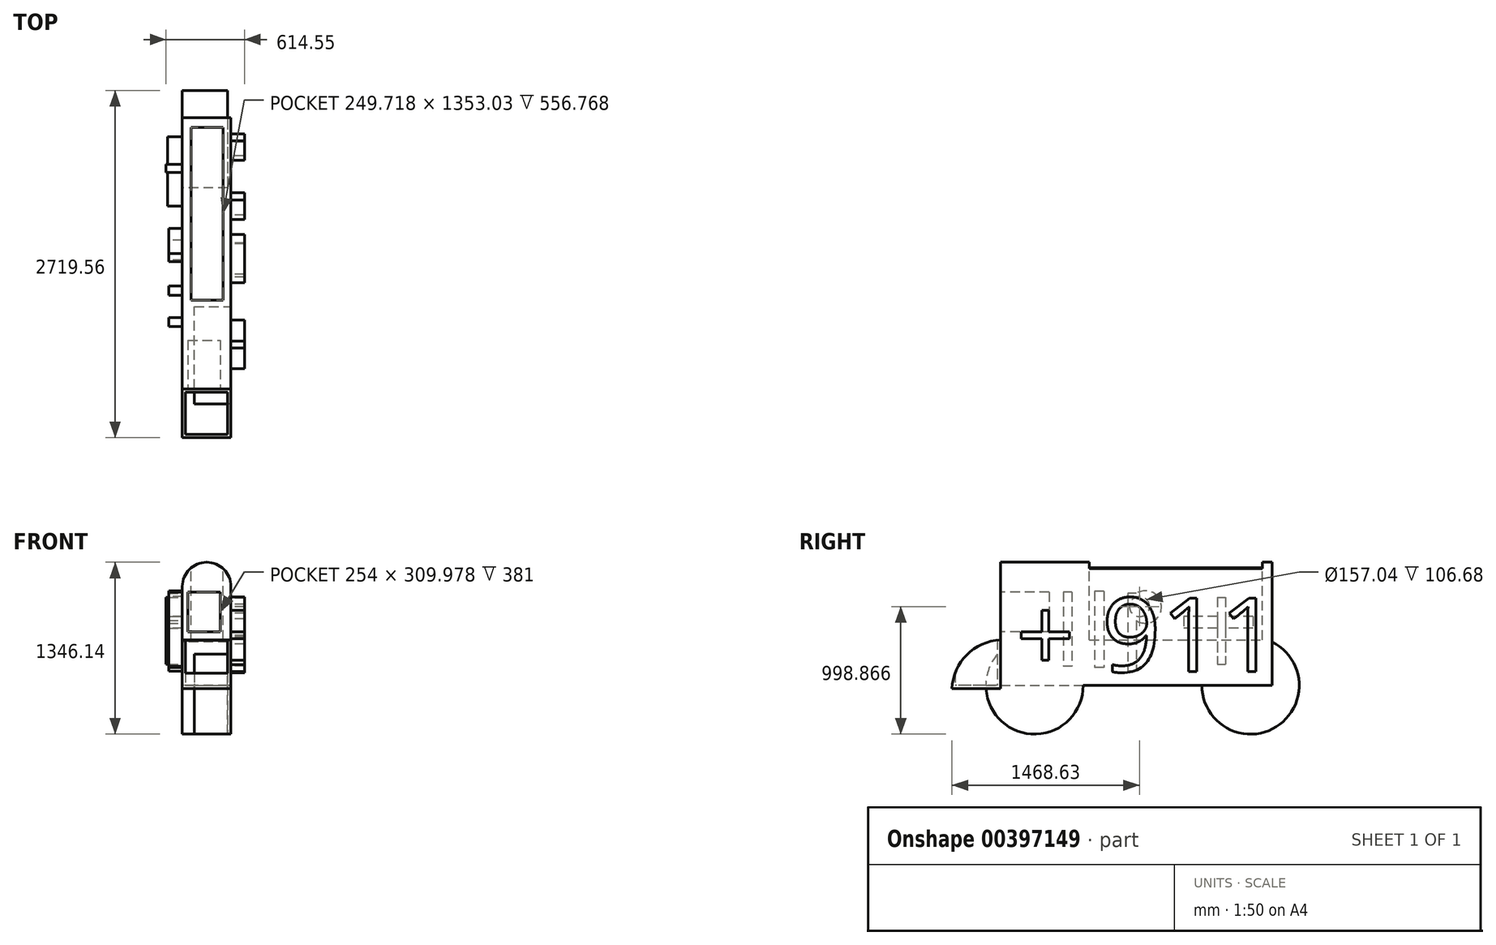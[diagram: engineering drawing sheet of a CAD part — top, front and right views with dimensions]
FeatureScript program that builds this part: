
annotation { "Feature Type Name" : "Feature", "Feature Type Description" : "" }
export const myFeature = defineFeature(function(context is Context, id is Id, definition is map)
    precondition{}
    {
        {
            var Q0;
            Q0=qCreatedBy(makeId("Top.planeOp"),FACE);
            var sketch = newSketch(context, id + "F0", { "sketchPlane" : qUnion([Q0])});
            skLineSegment(sketch, "E0.bottom", {"start": v(-196.72, 208.75) * mm, "end": v(184.28, 208.75) * mm});
            skLineSegment(sketch, "E0.top", {"start": v(-196.72, -172.25) * mm, "end": v(184.28, -172.25) * mm});
            skLineSegment(sketch, "E0.left", {"start": v(-196.72, 208.75) * mm, "end": v(-196.72, -172.25) * mm});
            skLineSegment(sketch, "E0.right", {"start": v(184.28, 208.75) * mm, "end": v(184.28, -172.25) * mm});
            skSolve(sketch);
        }
        {
            var Q0;
            Q0 = qSketchRegion(id + "F0", true);
            extrude(context, id + "F1", {"entities" : qUnion([Q0]), "depth" : 381 * mm});
        }
        {
            var Q0;
            Q0=makeQuery(id+"F1.opExtrude","CAP_FACE",FACE,{"disambiguationData":[OSD([sQuery(id+"F0.wireOp",EDGE,"E0.bottom"),sQuery(id+"F0.wireOp",EDGE,"E0.top"),sQuery(id+"F0.wireOp",EDGE,"E0.left"),sQuery(id+"F0.wireOp",EDGE,"E0.right")])],"isStart":false});
            shell(context, id + "F2", {"entities" : qUnion([Q0]), "thickness" : 25.4 * mm});
        }
        {
            var Q0;
            Q0=makeQuery(id+"F1.opExtrude","CAP_EDGE",EDGE,{"disambiguationData":[OSD([sQuery(id+"F0.wireOp",EDGE,"E0.top")])],"isStart":false});
            fillet(context, id + "F3", {"entities" : qUnion([Q0]), "radius" : 398.59 * mm, "tangentPropagation" : true, "allowEdgeOverflow" : false});
        }
        {
            var Q0;
            Q0=makeQuery(id+"F1.opExtrude","SWEPT_FACE",FACE,{"disambiguationData":[OSD([sQuery(id+"F0.wireOp",EDGE,"E0.bottom")])]});
            var sketch = newSketch(context, id + "F4", { "sketchPlane" : qUnion([Q0])});
            skLineSegment(sketch, "E1.bottom", {"start": v(-184.15, 990) * mm, "end": v(196.72, 990) * mm});
            skLineSegment(sketch, "E1.top", {"start": v(-184.15, 24.86) * mm, "end": v(196.72, 24.86) * mm});
            skLineSegment(sketch, "E1.left", {"start": v(-184.15, 990) * mm, "end": v(-184.15, 24.86) * mm});
            skLineSegment(sketch, "E1.right", {"start": v(196.72, 990) * mm, "end": v(196.72, 24.86) * mm});
            skSolve(sketch);
        }
        {
            var Q0;
            Q0 = qSketchRegion(id + "F4", true);
            extrude(context, id + "F5", {"entities" : qUnion([Q0]), "operationType" : NewBodyOperationType.ADD, "depth" : 93.98 * mm});
        }
        {
            var Q0;
            Q0=makeQuery(id+"F5.opExtrude","CAP_FACE",FACE,{"disambiguationData":[OSD([sQuery(id+"F4.wireOp",EDGE,"E1.bottom"),sQuery(id+"F4.wireOp",EDGE,"E1.top"),sQuery(id+"F4.wireOp",EDGE,"E1.left"),sQuery(id+"F4.wireOp",EDGE,"E1.right")])],"isStart":false});
            var sketch = newSketch(context, id + "F6", { "sketchPlane" : qUnion([Q0])});
            skLineSegment(sketch, "E2.bottom", {"start": v(-184.15, 990) * mm, "end": v(196.72, 990) * mm});
            skLineSegment(sketch, "E2.top", {"start": v(-184.15, 24.86) * mm, "end": v(196.72, 24.86) * mm});
            skLineSegment(sketch, "E2.left", {"start": v(-184.15, 990) * mm, "end": v(-184.15, 24.86) * mm});
            skLineSegment(sketch, "E2.right", {"start": v(196.72, 990) * mm, "end": v(196.72, 24.86) * mm});
            skSolve(sketch);
        }
        {
            var Q0;
            Q0 = qSketchRegion(id + "F6", true);
            extrude(context, id + "F7", {"entities" : qUnion([Q0]), "operationType" : NewBodyOperationType.ADD, "depth" : 2032 * mm});
        }
        {
            var Q0;
            Q0=makeQuery(id+"F7.boolean.opBoolean","MERGE",FACE,{"derivedFrom":[makeQuery(id+"F5.boolean.opBoolean","MERGE",FACE,{"derivedFrom":[makeQuery(id+"F1.opExtrude","SWEPT_FACE",FACE,{"disambiguationData":[OSD([sQuery(id+"F0.wireOp",EDGE,"E0.left")])]}),makeQuery(id+"F5.opExtrude","SWEPT_FACE",FACE,{"disambiguationData":[OSD([sQuery(id+"F4.wireOp",EDGE,"E1.right")])]})]}),makeQuery(id+"F7.opExtrude","SWEPT_FACE",FACE,{"disambiguationData":[OSD([sQuery(id+"F6.wireOp",EDGE,"E2.right")])]})]});
            var sketch = newSketch(context, id + "F8", { "sketchPlane" : qUnion([Q0])});
            skCircle(sketch, "E3", {"center": v(-2166.68, 24.86) * mm, "radius": 381 * mm});
            skSolve(sketch);
        }
        {
            var Q0;
            {var subQ0=sQuery(id+"F8.wireOp",EDGE,"E3");var subQ1=sQuery(id+"F6.wireOp",EDGE,"E2.right");var subQ2=makeQuery(id+"F7.opExtrude","CAP_EDGE",EDGE,{"disambiguationData":[OSD([subQ1])],"isStart":false});var subQ3=makeQuery(id+"F8.imprint","INTERSECT",VERTEX,{"derivedFrom":[subQ2,subQ0]});Q0=makeQuery(id+"F8.imprint","IMPRINT",FACE,{"disambiguationData":[TD([[makeQuery(id+"F8.imprint","IMPRINT",EDGE,{"disambiguationData":[TD([[subQ3,1.0]])],"derivedFrom":subQ0}),1.0]])]});}
            var Q1;
            {var subQ0=sQuery(id+"F8.wireOp",EDGE,"E3");var subQ1=sQuery(id+"F6.wireOp",EDGE,"E2.right");var subQ2=makeQuery(id+"F7.opExtrude","CAP_EDGE",EDGE,{"disambiguationData":[OSD([subQ1])],"isStart":false});var subQ3=makeQuery(id+"F8.imprint","INTERSECT",VERTEX,{"derivedFrom":[subQ2,subQ0]});Q1=makeQuery(id+"F8.imprint","IMPRINT",FACE,{"disambiguationData":[TD([[makeQuery(id+"F8.imprint","IMPRINT",EDGE,{"disambiguationData":[TD([[subQ3,-1.0]])],"derivedFrom":subQ0}),1.0]])]});}
            extrude(context, id + "F9", {"entities" : qUnion([Q0, Q1]), "operationType" : NewBodyOperationType.ADD, "oppositeDirection" : true, "depth" : 355.6 * mm});
        }
        {
            var Q0;
            Q0=makeQuery(id+"F7.boolean.opBoolean","MERGE",FACE,{"derivedFrom":[makeQuery(id+"F5.opExtrude","SWEPT_FACE",FACE,{"disambiguationData":[OSD([sQuery(id+"F4.wireOp",EDGE,"E1.left")])]}),makeQuery(id+"F7.opExtrude","SWEPT_FACE",FACE,{"disambiguationData":[OSD([sQuery(id+"F6.wireOp",EDGE,"E2.left")])]})]});
            var sketch = newSketch(context, id + "F10", { "sketchPlane" : qUnion([Q0])});
            skCircle(sketch, "E4", {"center": v(475.15, 24.86) * mm, "radius": 381 * mm});
            skSolve(sketch);
        }
        {
            var Q0;
            Q0 = qSketchRegion(id + "F10", true);
            extrude(context, id + "F11", {"entities" : qUnion([Q0]), "operationType" : NewBodyOperationType.ADD, "oppositeDirection" : true, "depth" : 287.02 * mm});
        }
        {
            var Q0;
            Q0=makeQuery(id+"F5.opExtrude","CAP_FACE",FACE,{"disambiguationData":[OSD([sQuery(id+"F4.wireOp",EDGE,"E1.bottom"),sQuery(id+"F4.wireOp",EDGE,"E1.top"),sQuery(id+"F4.wireOp",EDGE,"E1.left"),sQuery(id+"F4.wireOp",EDGE,"E1.right")])],"isStart":true});
            var sketch = newSketch(context, id + "F12", { "sketchPlane" : qUnion([Q0])});
            skLineSegment(sketch, "E5.bottom", {"start": v(-153.17, 756.16) * mm, "end": v(100.83, 756.16) * mm});
            skLineSegment(sketch, "E5.top", {"start": v(-153.17, 446.18) * mm, "end": v(100.83, 446.18) * mm});
            skLineSegment(sketch, "E5.left", {"start": v(-153.17, 756.16) * mm, "end": v(-153.17, 446.18) * mm});
            skLineSegment(sketch, "E5.right", {"start": v(100.83, 756.16) * mm, "end": v(100.83, 446.18) * mm});
            skSolve(sketch);
        }
        {
            var Q0;
            Q0 = qSketchRegion(id + "F12", true);
            extrude(context, id + "F13", {"entities" : qUnion([Q0]), "operationType" : NewBodyOperationType.REMOVE, "oppositeDirection" : true, "depth" : 381 * mm});
        }
        {
            var Q0;
            Q0=makeQuery(id+"F7.boolean.opBoolean","MERGE",FACE,{"derivedFrom":[makeQuery(id+"F5.opExtrude","SWEPT_FACE",FACE,{"disambiguationData":[OSD([sQuery(id+"F4.wireOp",EDGE,"E1.bottom")])]}),makeQuery(id+"F7.opExtrude","SWEPT_FACE",FACE,{"disambiguationData":[OSD([sQuery(id+"F6.wireOp",EDGE,"E2.bottom")])]})]});
            var sketch = newSketch(context, id + "F14", { "sketchPlane" : qUnion([Q0])});
            skLineSegment(sketch, "E6.bottom", {"start": v(-126.86, 904.82) * mm, "end": v(122.86, 904.82) * mm});
            skLineSegment(sketch, "E6.top", {"start": v(-126.86, 2257.84) * mm, "end": v(122.86, 2257.84) * mm});
            skLineSegment(sketch, "E6.left", {"start": v(-126.86, 904.82) * mm, "end": v(-126.86, 2257.84) * mm});
            skLineSegment(sketch, "E6.right", {"start": v(122.86, 904.82) * mm, "end": v(122.86, 2257.84) * mm});
            skSolve(sketch);
        }
        {
            var Q0;
            Q0=makeQuery(id+"F14.imprint","IMPRINT",FACE,{"disambiguationData":[TD([[makeQuery(id+"F14.imprint","IMPRINT",EDGE,{"derivedFrom":sQuery(id+"F14.wireOp",EDGE,"E6.bottom")}),1.0]])]});
            extrude(context, id + "F15", {"entities" : qUnion([Q0]), "operationType" : NewBodyOperationType.REMOVE, "oppositeDirection" : true, "depth" : 607.06 * mm});
        }
        {
            var Q0;
            Q0=makeQuery(id+"F7.boolean.opBoolean","MERGE",EDGE,{"derivedFrom":[makeQuery(id+"F5.opExtrude","SWEPT_EDGE",EDGE,{"disambiguationData":[OSD([sQuery(id+"F4.wireOp",EDGE,"E1.bottom"),sQuery(id+"F4.wireOp",EDGE,"E1.left")])]}),makeQuery(id+"F7.opExtrude","SWEPT_EDGE",EDGE,{"disambiguationData":[OSD([sQuery(id+"F6.wireOp",EDGE,"E2.bottom"),sQuery(id+"F6.wireOp",EDGE,"E2.left")])]})]});
            fillet(context, id + "F16", {"entities" : qUnion([Q0]), "radius" : 190.1 * mm, "tangentPropagation" : true, "allowEdgeOverflow" : false});
        }
        {
            var Q0;
            Q0=makeQuery(id+"F7.boolean.opBoolean","MERGE",EDGE,{"derivedFrom":[makeQuery(id+"F5.opExtrude","SWEPT_EDGE",EDGE,{"disambiguationData":[OSD([sQuery(id+"F4.wireOp",EDGE,"E1.bottom"),sQuery(id+"F4.wireOp",EDGE,"E1.right")])]}),makeQuery(id+"F7.opExtrude","SWEPT_EDGE",EDGE,{"disambiguationData":[OSD([sQuery(id+"F6.wireOp",EDGE,"E2.bottom"),sQuery(id+"F6.wireOp",EDGE,"E2.right")])]})]});
            fillet(context, id + "F17", {"entities" : qUnion([Q0]), "radius" : 190.1 * mm, "tangentPropagation" : true, "allowEdgeOverflow" : false});
        }
        {
            var Q0;
            Q0=makeQuery(id+"F9.boolean.opBoolean","MERGE",FACE,{"derivedFrom":[makeQuery(id+"F7.boolean.opBoolean","MERGE",FACE,{"derivedFrom":[makeQuery(id+"F5.boolean.opBoolean","MERGE",FACE,{"derivedFrom":[makeQuery(id+"F1.opExtrude","SWEPT_FACE",FACE,{"disambiguationData":[OSD([sQuery(id+"F0.wireOp",EDGE,"E0.left")])]}),makeQuery(id+"F5.opExtrude","SWEPT_FACE",FACE,{"disambiguationData":[OSD([sQuery(id+"F4.wireOp",EDGE,"E1.right")])]})]}),makeQuery(id+"F7.opExtrude","SWEPT_FACE",FACE,{"disambiguationData":[OSD([sQuery(id+"F6.wireOp",EDGE,"E2.right")])]})]}),makeQuery(id+"F9.opExtrude","CAP_FACE",FACE,{"disambiguationData":[OSD([sQuery(id+"F8.wireOp",EDGE,"E3")])],"isStart":true})]});
            var sketch = newSketch(context, id + "F18", { "sketchPlane" : qUnion([Q0])});
            skLineSegment(sketch, "E7.bottom", {"start": v(-1906.79, 715.19) * mm, "end": v(-1970.29, 715.19) * mm});
            skLineSegment(sketch, "E7.top", {"start": v(-1906.79, 189.64) * mm, "end": v(-1970.29, 189.64) * mm});
            skLineSegment(sketch, "E7.left", {"start": v(-1906.79, 715.19) * mm, "end": v(-1906.79, 189.64) * mm});
            skLineSegment(sketch, "E7.right", {"start": v(-1970.29, 715.19) * mm, "end": v(-1970.29, 189.64) * mm});
            skSolve(sketch);
        }
        {
            var Q0;
            Q0=makeQuery(id+"F18.imprint","IMPRINT",FACE,{"disambiguationData":[TD([[makeQuery(id+"F18.imprint","IMPRINT",EDGE,{"derivedFrom":sQuery(id+"F18.wireOp",EDGE,"E7.bottom")}),1.0]])]});
            extrude(context, id + "F19", {"entities" : qUnion([Q0]), "operationType" : NewBodyOperationType.ADD, "depth" : 127 * mm});
        }
        {
            var Q0;
            Q0=makeQuery(id+"F9.boolean.opBoolean","MERGE",FACE,{"derivedFrom":[makeQuery(id+"F7.boolean.opBoolean","MERGE",FACE,{"derivedFrom":[makeQuery(id+"F5.boolean.opBoolean","MERGE",FACE,{"derivedFrom":[makeQuery(id+"F1.opExtrude","SWEPT_FACE",FACE,{"disambiguationData":[OSD([sQuery(id+"F0.wireOp",EDGE,"E0.left")])]}),makeQuery(id+"F5.opExtrude","SWEPT_FACE",FACE,{"disambiguationData":[OSD([sQuery(id+"F4.wireOp",EDGE,"E1.right")])]})]}),makeQuery(id+"F7.opExtrude","SWEPT_FACE",FACE,{"disambiguationData":[OSD([sQuery(id+"F6.wireOp",EDGE,"E2.right")])]})]}),makeQuery(id+"F9.opExtrude","CAP_FACE",FACE,{"disambiguationData":[OSD([sQuery(id+"F8.wireOp",EDGE,"E3")])],"isStart":true})]});
            var sketch = newSketch(context, id + "F20", { "sketchPlane" : qUnion([Q0])});
            skLineSegment(sketch, "E8.bottom", {"start": v(-2185.65, 565.2) * mm, "end": v(-1643.19, 565.2) * mm});
            skLineSegment(sketch, "E8.top", {"start": v(-2185.65, 473.85) * mm, "end": v(-1643.19, 473.85) * mm});
            skLineSegment(sketch, "E8.left", {"start": v(-2185.65, 565.2) * mm, "end": v(-2185.65, 473.85) * mm});
            skLineSegment(sketch, "E8.right", {"start": v(-1643.19, 565.2) * mm, "end": v(-1643.19, 473.85) * mm});
            skSolve(sketch);
        }
        {
            var Q0;
            Q0 = qSketchRegion(id + "F20", true);
            extrude(context, id + "F21", {"entities" : qUnion([Q0]), "operationType" : NewBodyOperationType.ADD, "depth" : 114.3 * mm});
        }
        {
            var Q0;
            Q0=makeQuery(id+"F9.boolean.opBoolean","MERGE",FACE,{"derivedFrom":[makeQuery(id+"F7.boolean.opBoolean","MERGE",FACE,{"derivedFrom":[makeQuery(id+"F5.boolean.opBoolean","MERGE",FACE,{"derivedFrom":[makeQuery(id+"F1.opExtrude","SWEPT_FACE",FACE,{"disambiguationData":[OSD([sQuery(id+"F0.wireOp",EDGE,"E0.left")])]}),makeQuery(id+"F5.opExtrude","SWEPT_FACE",FACE,{"disambiguationData":[OSD([sQuery(id+"F4.wireOp",EDGE,"E1.right")])]})]}),makeQuery(id+"F7.opExtrude","SWEPT_FACE",FACE,{"disambiguationData":[OSD([sQuery(id+"F6.wireOp",EDGE,"E2.right")])]})]}),makeQuery(id+"F9.opExtrude","CAP_FACE",FACE,{"disambiguationData":[OSD([sQuery(id+"F8.wireOp",EDGE,"E3")])],"isStart":true})]});
            var sketch = newSketch(context, id + "F22", { "sketchPlane" : qUnion([Q0])});
            skLineSegment(sketch, "E9.bottom", {"start": v(-1271.82, 747.9) * mm, "end": v(-1206, 747.9) * mm});
            skLineSegment(sketch, "E9.top", {"start": v(-1271.82, 137.29) * mm, "end": v(-1206, 137.29) * mm});
            skLineSegment(sketch, "E9.left", {"start": v(-1271.82, 747.9) * mm, "end": v(-1271.82, 137.29) * mm});
            skLineSegment(sketch, "E9.right", {"start": v(-1206, 747.9) * mm, "end": v(-1206, 137.29) * mm});
            skSolve(sketch);
        }
        {
            var Q0;
            Q0 = qSketchRegion(id + "F22", true);
            extrude(context, id + "F23", {"entities" : qUnion([Q0]), "operationType" : NewBodyOperationType.ADD, "depth" : 106.68 * mm});
        }
        {
            var Q0;
            Q0=makeQuery(id+"F9.boolean.opBoolean","MERGE",FACE,{"derivedFrom":[makeQuery(id+"F7.boolean.opBoolean","MERGE",FACE,{"derivedFrom":[makeQuery(id+"F5.boolean.opBoolean","MERGE",FACE,{"derivedFrom":[makeQuery(id+"F1.opExtrude","SWEPT_FACE",FACE,{"disambiguationData":[OSD([sQuery(id+"F0.wireOp",EDGE,"E0.left")])]}),makeQuery(id+"F5.opExtrude","SWEPT_FACE",FACE,{"disambiguationData":[OSD([sQuery(id+"F4.wireOp",EDGE,"E1.right")])]})]}),makeQuery(id+"F7.opExtrude","SWEPT_FACE",FACE,{"disambiguationData":[OSD([sQuery(id+"F6.wireOp",EDGE,"E2.right")])]})]}),makeQuery(id+"F9.opExtrude","CAP_FACE",FACE,{"disambiguationData":[OSD([sQuery(id+"F8.wireOp",EDGE,"E3")])],"isStart":true})]});
            var sketch = newSketch(context, id + "F24", { "sketchPlane" : qUnion([Q0])});
            skCircle(sketch, "E10", {"center": v(-1341.75, 639.8) * mm, "radius": 127 * mm});
            skSolve(sketch);
        }
        {
            var Q0;
            Q0 = qSketchRegion(id + "F24", true);
            extrude(context, id + "F25", {"entities" : qUnion([Q0]), "operationType" : NewBodyOperationType.ADD, "depth" : 106.68 * mm});
        }
        {
            var Q0;
            Q0=makeQuery(id+"F25.boolean.opBoolean","MERGE",FACE,{"derivedFrom":[makeQuery(id+"F23.opExtrude","CAP_FACE",FACE,{"disambiguationData":[OSD([sQuery(id+"F22.wireOp",EDGE,"E9.bottom"),sQuery(id+"F22.wireOp",EDGE,"E9.top"),sQuery(id+"F22.wireOp",EDGE,"E9.left"),sQuery(id+"F22.wireOp",EDGE,"E9.right")])],"isStart":false}),makeQuery(id+"F25.opExtrude","CAP_FACE",FACE,{"disambiguationData":[OSD([sQuery(id+"F24.wireOp",EDGE,"E10")])],"isStart":false})]});
            var sketch = newSketch(context, id + "F26", { "sketchPlane" : qUnion([Q0])});
            skCircle(sketch, "E11", {"center": v(-1296.75, 642.73) * mm, "radius": 78.52 * mm});
            skSolve(sketch);
        }
        {
            var Q0;
            Q0 = qSketchRegion(id + "F26", true);
            extrude(context, id + "F27", {"entities" : qUnion([Q0]), "operationType" : NewBodyOperationType.REMOVE, "oppositeDirection" : true, "depth" : 106.68 * mm});
        }
        {
            var Q0;
            Q0=makeQuery(id+"F9.boolean.opBoolean","MERGE",FACE,{"derivedFrom":[makeQuery(id+"F7.boolean.opBoolean","MERGE",FACE,{"derivedFrom":[makeQuery(id+"F5.boolean.opBoolean","MERGE",FACE,{"derivedFrom":[makeQuery(id+"F1.opExtrude","SWEPT_FACE",FACE,{"disambiguationData":[OSD([sQuery(id+"F0.wireOp",EDGE,"E0.left")])]}),makeQuery(id+"F5.opExtrude","SWEPT_FACE",FACE,{"disambiguationData":[OSD([sQuery(id+"F4.wireOp",EDGE,"E1.right")])]})]}),makeQuery(id+"F7.opExtrude","SWEPT_FACE",FACE,{"disambiguationData":[OSD([sQuery(id+"F6.wireOp",EDGE,"E2.right")])]})]}),makeQuery(id+"F9.opExtrude","CAP_FACE",FACE,{"disambiguationData":[OSD([sQuery(id+"F8.wireOp",EDGE,"E3")])],"isStart":true})]});
            var sketch = newSketch(context, id + "F28", { "sketchPlane" : qUnion([Q0])});
            skLineSegment(sketch, "E12.bottom", {"start": v(-1016.58, 761.18) * mm, "end": v(-944.28, 761.18) * mm});
            skLineSegment(sketch, "E12.top", {"start": v(-1016.58, 166.55) * mm, "end": v(-944.28, 166.55) * mm});
            skLineSegment(sketch, "E12.left", {"start": v(-1016.58, 761.18) * mm, "end": v(-1016.58, 166.55) * mm});
            skLineSegment(sketch, "E12.right", {"start": v(-944.28, 761.18) * mm, "end": v(-944.28, 166.55) * mm});
            skSolve(sketch);
        }
        {
            var Q0;
            Q0 = qSketchRegion(id + "F28", true);
            extrude(context, id + "F29", {"entities" : qUnion([Q0]), "operationType" : NewBodyOperationType.ADD, "depth" : 106.68 * mm});
        }
        {
            var Q0;
            Q0=makeQuery(id+"F9.boolean.opBoolean","MERGE",FACE,{"derivedFrom":[makeQuery(id+"F7.boolean.opBoolean","MERGE",FACE,{"derivedFrom":[makeQuery(id+"F5.boolean.opBoolean","MERGE",FACE,{"derivedFrom":[makeQuery(id+"F1.opExtrude","SWEPT_FACE",FACE,{"disambiguationData":[OSD([sQuery(id+"F0.wireOp",EDGE,"E0.left")])]}),makeQuery(id+"F5.opExtrude","SWEPT_FACE",FACE,{"disambiguationData":[OSD([sQuery(id+"F4.wireOp",EDGE,"E1.right")])]})]}),makeQuery(id+"F7.opExtrude","SWEPT_FACE",FACE,{"disambiguationData":[OSD([sQuery(id+"F6.wireOp",EDGE,"E2.right")])]})]}),makeQuery(id+"F9.opExtrude","CAP_FACE",FACE,{"disambiguationData":[OSD([sQuery(id+"F8.wireOp",EDGE,"E3")])],"isStart":true})]});
            var sketch = newSketch(context, id + "F30", { "sketchPlane" : qUnion([Q0])});
            skLineSegment(sketch, "E13.bottom", {"start": v(-767.57, 756.04) * mm, "end": v(-699, 756.04) * mm});
            skLineSegment(sketch, "E13.top", {"start": v(-767.57, 175.61) * mm, "end": v(-699, 175.61) * mm});
            skLineSegment(sketch, "E13.left", {"start": v(-767.57, 756.04) * mm, "end": v(-767.57, 175.61) * mm});
            skLineSegment(sketch, "E13.right", {"start": v(-699, 756.04) * mm, "end": v(-699, 175.61) * mm});
            skSolve(sketch);
        }
        {
            var Q0;
            Q0 = qSketchRegion(id + "F30", true);
            extrude(context, id + "F31", {"entities" : qUnion([Q0]), "operationType" : NewBodyOperationType.ADD, "depth" : 106.68 * mm});
        }
        {
            var Q0;
            Q0=makeQuery(id+"F11.boolean.opBoolean","MERGE",FACE,{"derivedFrom":[makeQuery(id+"F7.boolean.opBoolean","MERGE",FACE,{"derivedFrom":[makeQuery(id+"F5.opExtrude","SWEPT_FACE",FACE,{"disambiguationData":[OSD([sQuery(id+"F4.wireOp",EDGE,"E1.left")])]}),makeQuery(id+"F7.opExtrude","SWEPT_FACE",FACE,{"disambiguationData":[OSD([sQuery(id+"F6.wireOp",EDGE,"E2.left")])]})]}),makeQuery(id+"F11.opExtrude","CAP_FACE",FACE,{"disambiguationData":[OSD([sQuery(id+"F10.wireOp",EDGE,"E4")])],"isStart":true})]});
            var sketch = newSketch(context, id + "F32", { "sketchPlane" : qUnion([Q0])});
            skText(sketch, "E14", { "text": "+ 911", "fontName": "OpenSans-Regular.ttf"});
            const initialGuessF32  = {"E14": [0.32832, 0.13257, 1, 0, 0.58248]};
            skSetInitialGuess(sketch, initialGuessF32);
            skSolve(sketch);
        }
        {
            var Q0;
            Q0 = qSketchRegion(id + "F32", true);
            extrude(context, id + "F33", {"entities" : qUnion([Q0]), "operationType" : NewBodyOperationType.ADD, "depth" : 106.68 * mm});
        }
    });
